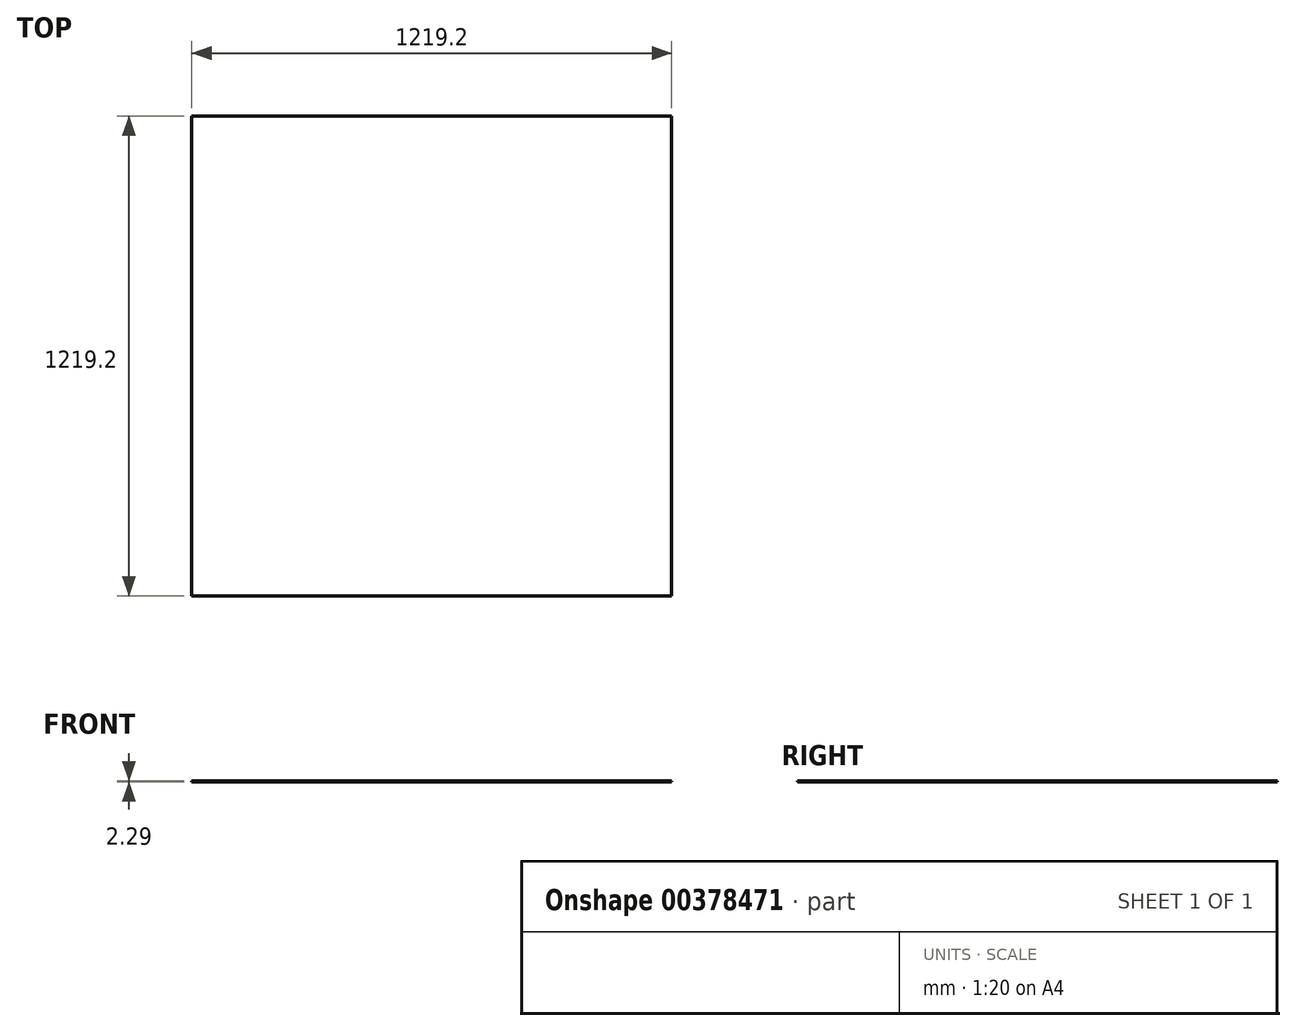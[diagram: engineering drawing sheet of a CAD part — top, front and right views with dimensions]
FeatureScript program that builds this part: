
annotation { "Feature Type Name" : "Feature", "Feature Type Description" : "" }
export const myFeature = defineFeature(function(context is Context, id is Id, definition is map)
    precondition{}
    {
        {
            var Q0;
            Q0=qCreatedBy(makeId("Top.planeOp"),FACE);
            var sketch = newSketch(context, id + "F0", { "sketchPlane" : qUnion([Q0])});
            skLineSegment(sketch, "E0.bottom", {"start": v(-609.6, 609.6) * mm, "end": v(609.6, 609.6) * mm});
            skLineSegment(sketch, "E0.top", {"start": v(-609.6, -609.6) * mm, "end": v(609.6, -609.6) * mm});
            skLineSegment(sketch, "E0.left", {"start": v(-609.6, 609.6) * mm, "end": v(-609.6, -609.6) * mm});
            skLineSegment(sketch, "E0.right", {"start": v(609.6, 609.6) * mm, "end": v(609.6, -609.6) * mm});
            skPoint(sketch, "E0.middle", {"position": v(0, 0) * mm});
            skSolve(sketch);
        }
        {
            var Q0;
            Q0 = qSketchRegion(id + "F0", true);
            extrude(context, id + "F1", {"entities" : qUnion([Q0]), "depth" : 2.3 * mm});
        }
    });
